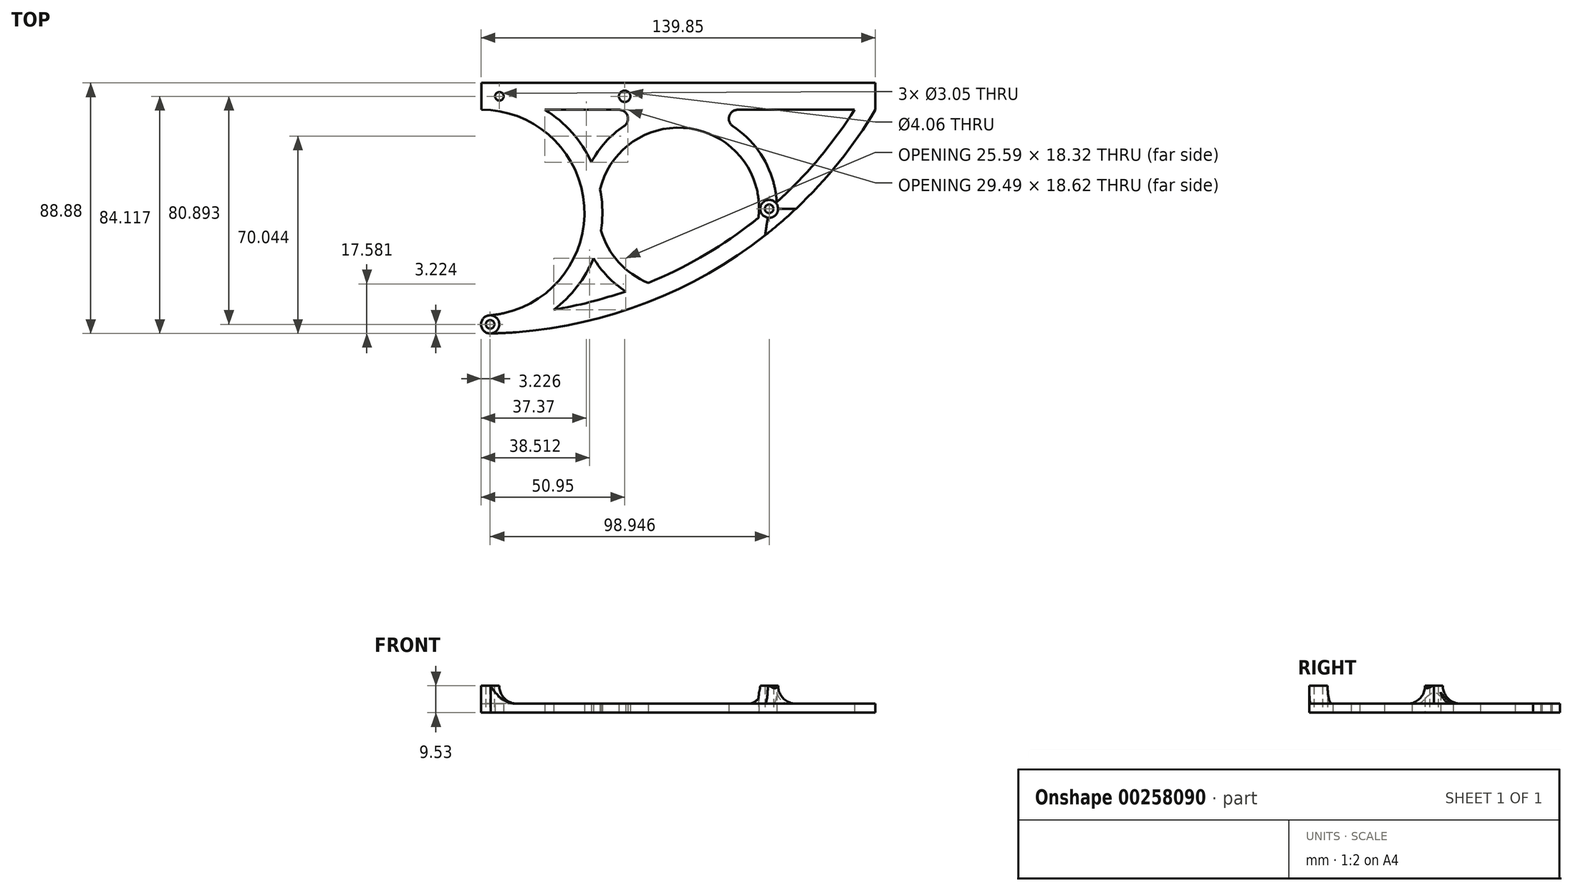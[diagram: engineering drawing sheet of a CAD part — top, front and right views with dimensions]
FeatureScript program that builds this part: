
annotation { "Feature Type Name" : "Feature", "Feature Type Description" : "" }
export const myFeature = defineFeature(function(context is Context, id is Id, definition is map)
    precondition{}
    {
        {
            var Q0;
            Q0=qCreatedBy(makeId("Top.planeOp"),FACE);
            var sketch = newSketch(context, id + "F0", { "sketchPlane" : qUnion([Q0])});
            skPoint(sketch, "E0.middle", {"position": v(0, 0) * mm});
            skLineSegment(sketch, "E1.bottom", {"start": v(-69.85, 44.45) * mm, "end": v(69.85, 44.45) * mm});
            skLineSegment(sketch, "E1.left", {"start": v(-69.85, 44.45) * mm, "end": v(-69.85, 34.92) * mm});
            skLineSegment(sketch, "E1.right", {"start": v(69.85, 44.45) * mm, "end": v(69.85, 34.93) * mm});
            skLineSegment(sketch, "E2", {"start": v(-47.37, 34.92) * mm, "end": v(-21.06, 34.92) * mm});
            skPoint(sketch, "E3", {"position": v(-69.85, -44.45) * mm});
            skArc(sketch, "E4", {"start": v(-66.62, -44.43) * mm, "mid": v(11.9, -22.42) * mm, "end": v(69.85, 34.93) * mm});
            skLineSegment(sketch, "E5", {"start": v(-69.85, -41.25) * mm, "end": v(-69.85, -41.15) * mm});
            skArc(sketch, "E6", {"start": v(-66.93, -37.98) * mm, "mid": v(-33.37, -0.13) * mm, "end": v(-69.85, 34.92) * mm});
            skArc(sketch, "E7", {"start": v(-44.29, -36) * mm, "mid": v(-31.35, -33.3) * mm, "end": v(-18.7, -29.5) * mm});
            skArc(sketch, "E8.trimOffspring", {"start": v(-44.29, -36) * mm, "mid": v(-35.94, -27.82) * mm, "end": v(-30.11, -17.69) * mm});
            skPoint(sketch, "E9.visualSharp", {"position": v(-69.85, -38.1) * mm});
            skArc(sketch, "E10", {"start": v(-30.11, -17.69) * mm, "mid": v(-25.1, -24.28) * mm, "end": v(-18.7, -29.5) * mm});
            skArc(sketch, "E11.trimOffspring", {"start": v(-19.3, 29.1) * mm, "mid": v(-25.9, 23.43) * mm, "end": v(-30.89, 16.3) * mm});
            skArc(sketch, "E12", {"start": v(-27.45, -7.94) * mm, "mid": v(-21.21, -19.14) * mm, "end": v(-10.71, -26.5) * mm});
            skArc(sketch, "E13.trimOffspring", {"start": v(28.37, -3.39) * mm, "mid": v(5.05, 28.13) * mm, "end": v(-27.78, 6.69) * mm});
            skArc(sketch, "E14.filletArc", {"start": v(-19.3, 29.1) * mm, "mid": v(-18.02, 32.67) * mm, "end": v(-21.06, 34.92) * mm});
            skArc(sketch, "E15", {"start": v(34.86, 2.15) * mm, "mid": v(30.25, 17.45) * mm, "end": v(19.3, 29.1) * mm});
            skLineSegment(sketch, "E16", {"start": v(21.06, 34.92) * mm, "end": v(62.42, 34.93) * mm});
            skArc(sketch, "E17.filletArc", {"start": v(21.06, 34.92) * mm, "mid": v(18.02, 32.67) * mm, "end": v(19.3, 29.1) * mm});
            skArc(sketch, "E18.trimOffspring", {"start": v(-27.45, -7.94) * mm, "mid": v(-26.99, -0.61) * mm, "end": v(-27.78, 6.69) * mm});
            skArc(sketch, "E19.trimOffspring", {"start": v(-30.89, 16.3) * mm, "mid": v(-37.75, 26.84) * mm, "end": v(-47.37, 34.92) * mm});
            skArc(sketch, "E20.trimOffspring", {"start": v(34.86, 2.15) * mm, "mid": v(49.77, 17.59) * mm, "end": v(62.42, 34.93) * mm});
            skArc(sketch, "E21.trimOffspring", {"start": v(-10.71, -26.5) * mm, "mid": v(9.67, -16.37) * mm, "end": v(28.37, -3.39) * mm});
            skArc(sketch, "E22", {"start": v(-66.93, -37.98) * mm, "mid": v(-70, -41.36) * mm, "end": v(-66.62, -44.43) * mm});
            skSolve(sketch);
        }
        {
            var Q0;
            Q0 = qSketchRegion(id + "F0", true);
            extrude(context, id + "F1", {"entities" : qUnion([Q0]), "depth" : 3.17 * mm});
        }
        {
            var Q0;
            Q0=makeQuery(id+"F0.imprint","IMPRINT",FACE,{"disambiguationData":[TD([[makeQuery(id+"F0.imprint","IMPRINT",EDGE,{"derivedFrom":sQuery(id+"F0.wireOp",EDGE,"E1.bottom")}),-1.0]])]});
            var sketch = newSketch(context, id + "F2", { "sketchPlane" : qUnion([Q0])});
            skLineSegment(sketch, "E23.0", {"start": v(-69.85, 44.45) * mm, "end": v(-69.85, 34.92) * mm, "construction": true});
            skLineSegment(sketch, "E23.1", {"start": v(69.85, 44.45) * mm, "end": v(69.85, 34.93) * mm, "construction": true});
            skPoint(sketch, "E23.2", {"position": v(-69.85, 39.69) * mm});
            skPoint(sketch, "E23.3", {"position": v(69.85, 39.69) * mm});
            skLineSegment(sketch, "E24", {"start": v(-69.85, 39.69) * mm, "end": v(-63.5, 39.69) * mm, "construction": true});
            skArc(sketch, "E25.0", {"start": v(34.86, 2.15) * mm, "mid": v(49.77, 17.59) * mm, "end": v(62.42, 34.93) * mm, "construction": true});
            skArc(sketch, "E25.1", {"start": v(-10.71, -26.5) * mm, "mid": v(9.67, -16.37) * mm, "end": v(28.37, -3.39) * mm, "construction": true});
            skArc(sketch, "E26.0", {"start": v(28.37, -3.39) * mm, "mid": v(5.05, 28.13) * mm, "end": v(-27.78, 6.69) * mm, "construction": true});
            skCircle(sketch, "E27", {"center": v(32.17, -0.21) * mm, "radius": 3.18 * mm});
            skArc(sketch, "E28.0", {"start": v(-66.93, -37.98) * mm, "mid": v(-70, -41.36) * mm, "end": v(-66.62, -44.43) * mm, "construction": true});
            skCircle(sketch, "E29", {"center": v(-66.77, -41.2) * mm, "radius": 3.23 * mm});
            skSolve(sketch);
        }
        {
            var Q0;
            Q0 = qSketchRegion(id + "F2", true);
            extrude(context, id + "F3", {"entities" : qUnion([Q0]), "operationType" : NewBodyOperationType.ADD, "depth" : 9.52 * mm});
        }
        {
            var Q0;
            Q0=qCreatedBy(makeId("Top.planeOp"),FACE);
            var sketch = newSketch(context, id + "F4", { "sketchPlane" : qUnion([Q0])});
            skCircle(sketch, "E30", {"center": v(32.17, -0.21) * mm, "radius": 1.52 * mm});
            skLineSegment(sketch, "E31.0", {"start": v(-69.85, 39.69) * mm, "end": v(-63.5, 39.69) * mm, "construction": true});
            skCircle(sketch, "E32", {"center": v(-63.5, 39.69) * mm, "radius": 1.52 * mm});
            skLineSegment(sketch, "E33", {"start": v(-69.85, 39.69) * mm, "end": v(-19.05, 39.69) * mm, "construction": true});
            skCircle(sketch, "E34", {"center": v(-19.05, 39.69) * mm, "radius": 2.03 * mm});
            skCircle(sketch, "E35.0", {"center": v(-66.77, -41.2) * mm, "radius": 3.23 * mm, "construction": true});
            skCircle(sketch, "E36", {"center": v(-66.77, -41.2) * mm, "radius": 1.52 * mm});
            skSolve(sketch);
        }
        {
            var Q0;
            Q0 = qSketchRegion(id + "F4", true);
            extrude(context, id + "F5", {"entities" : qUnion([Q0]), "operationType" : NewBodyOperationType.REMOVE, "depth" : 25.4 * mm});
        }
        {
            var Q0;
            Q0=makeQuery(id+"F3.boolean.opBoolean","INTERSECT",EDGE,{"derivedFrom":[makeQuery(id+"F1.opExtrude","CAP_FACE",FACE,{"disambiguationData":[OSD([sQuery(id+"F0.wireOp",EDGE,"E1.bottom"),sQuery(id+"F0.wireOp",EDGE,"E1.left"),sQuery(id+"F0.wireOp",EDGE,"E1.right"),sQuery(id+"F0.wireOp",EDGE,"E2"),sQuery(id+"F0.wireOp",EDGE,"E4"),sQuery(id+"F0.wireOp",EDGE,"E6"),sQuery(id+"F0.wireOp",EDGE,"E7"),sQuery(id+"F0.wireOp",EDGE,"E8.trimOffspring"),sQuery(id+"F0.wireOp",EDGE,"E11.trimOffspring"),sQuery(id+"F0.wireOp",EDGE,"E12"),sQuery(id+"F0.wireOp",EDGE,"E13.trimOffspring"),sQuery(id+"F0.wireOp",EDGE,"E14.filletArc"),sQuery(id+"F0.wireOp",EDGE,"E15"),sQuery(id+"F0.wireOp",EDGE,"E10"),sQuery(id+"F0.wireOp",EDGE,"E16"),sQuery(id+"F0.wireOp",EDGE,"E17.filletArc"),sQuery(id+"F0.wireOp",EDGE,"E18.trimOffspring"),sQuery(id+"F0.wireOp",EDGE,"E19.trimOffspring"),sQuery(id+"F0.wireOp",EDGE,"E20.trimOffspring"),sQuery(id+"F0.wireOp",EDGE,"E21.trimOffspring"),sQuery(id+"F0.wireOp",EDGE,"E22")])],"isStart":false}),makeQuery(id+"F3.opExtrude","SWEPT_FACE",FACE,{"disambiguationData":[OSD([sQuery(id+"F2.wireOp",EDGE,"E29")])]})]});
            fillet(context, id + "F6", {"entities" : qUnion([Q0]), "radius" : 6.35 * mm, "tangentPropagation" : true, "allowEdgeOverflow" : false});
        }
        {
            var Q0;
            Q0=makeQuery(id+"F3.boolean.opBoolean","INTERSECT",EDGE,{"derivedFrom":[makeQuery(id+"F1.opExtrude","CAP_FACE",FACE,{"disambiguationData":[OSD([sQuery(id+"F0.wireOp",EDGE,"E1.bottom"),sQuery(id+"F0.wireOp",EDGE,"E1.left"),sQuery(id+"F0.wireOp",EDGE,"E1.right"),sQuery(id+"F0.wireOp",EDGE,"E2"),sQuery(id+"F0.wireOp",EDGE,"E4"),sQuery(id+"F0.wireOp",EDGE,"E6"),sQuery(id+"F0.wireOp",EDGE,"E7"),sQuery(id+"F0.wireOp",EDGE,"E8.trimOffspring"),sQuery(id+"F0.wireOp",EDGE,"E11.trimOffspring"),sQuery(id+"F0.wireOp",EDGE,"E12"),sQuery(id+"F0.wireOp",EDGE,"E13.trimOffspring"),sQuery(id+"F0.wireOp",EDGE,"E14.filletArc"),sQuery(id+"F0.wireOp",EDGE,"E15"),sQuery(id+"F0.wireOp",EDGE,"E10"),sQuery(id+"F0.wireOp",EDGE,"E16"),sQuery(id+"F0.wireOp",EDGE,"E17.filletArc"),sQuery(id+"F0.wireOp",EDGE,"E18.trimOffspring"),sQuery(id+"F0.wireOp",EDGE,"E19.trimOffspring"),sQuery(id+"F0.wireOp",EDGE,"E20.trimOffspring"),sQuery(id+"F0.wireOp",EDGE,"E21.trimOffspring"),sQuery(id+"F0.wireOp",EDGE,"E22")])],"isStart":false}),makeQuery(id+"F3.opExtrude","SWEPT_FACE",FACE,{"disambiguationData":[OSD([sQuery(id+"F2.wireOp",EDGE,"E27")])]})]});
            fillet(context, id + "F7", {"entities" : qUnion([Q0]), "radius" : 6.35 * mm, "tangentPropagation" : true, "allowEdgeOverflow" : false});
        }
    });
